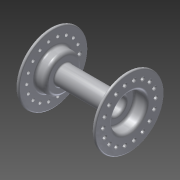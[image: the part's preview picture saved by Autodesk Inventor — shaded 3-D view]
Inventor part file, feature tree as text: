
AUTODESK INVENTOR PART (.ipt)
format: ipt  version: 2015 (Build 190159000, 159)  size: 399,360 bytes
history: native  units: mm
features: other x2, chamfer x2, sketch x2, hole x1, pattern_circular x1
ambient origin geometry x8: Origin, YZ Plane, XZ Plane, XY Plane, X Axis, Y Axis, Z Axis, Center Point
bodies: Body1 (feature_tree)
feature tree (8):
  other  "Bryła1"
  other  "Piasta"
  hole  "Otwór na szprychę"  [1 undecoded]
  chamfer  "Faza1"  Distance=1.0mm
  chamfer  "Faza2"  Angle=90.0deg  [1 undecoded]
  pattern_circular  "Szyk otworów na szprychy"  [2 undecoded]
  sketch  "Szkic1"
  sketch  "Szkic2"
note: 4 required parameter values undecoded (feature->parameter linkage not recoverable at this tier; creation-order binding heuristic only, values carry confidence <= 0.55)
